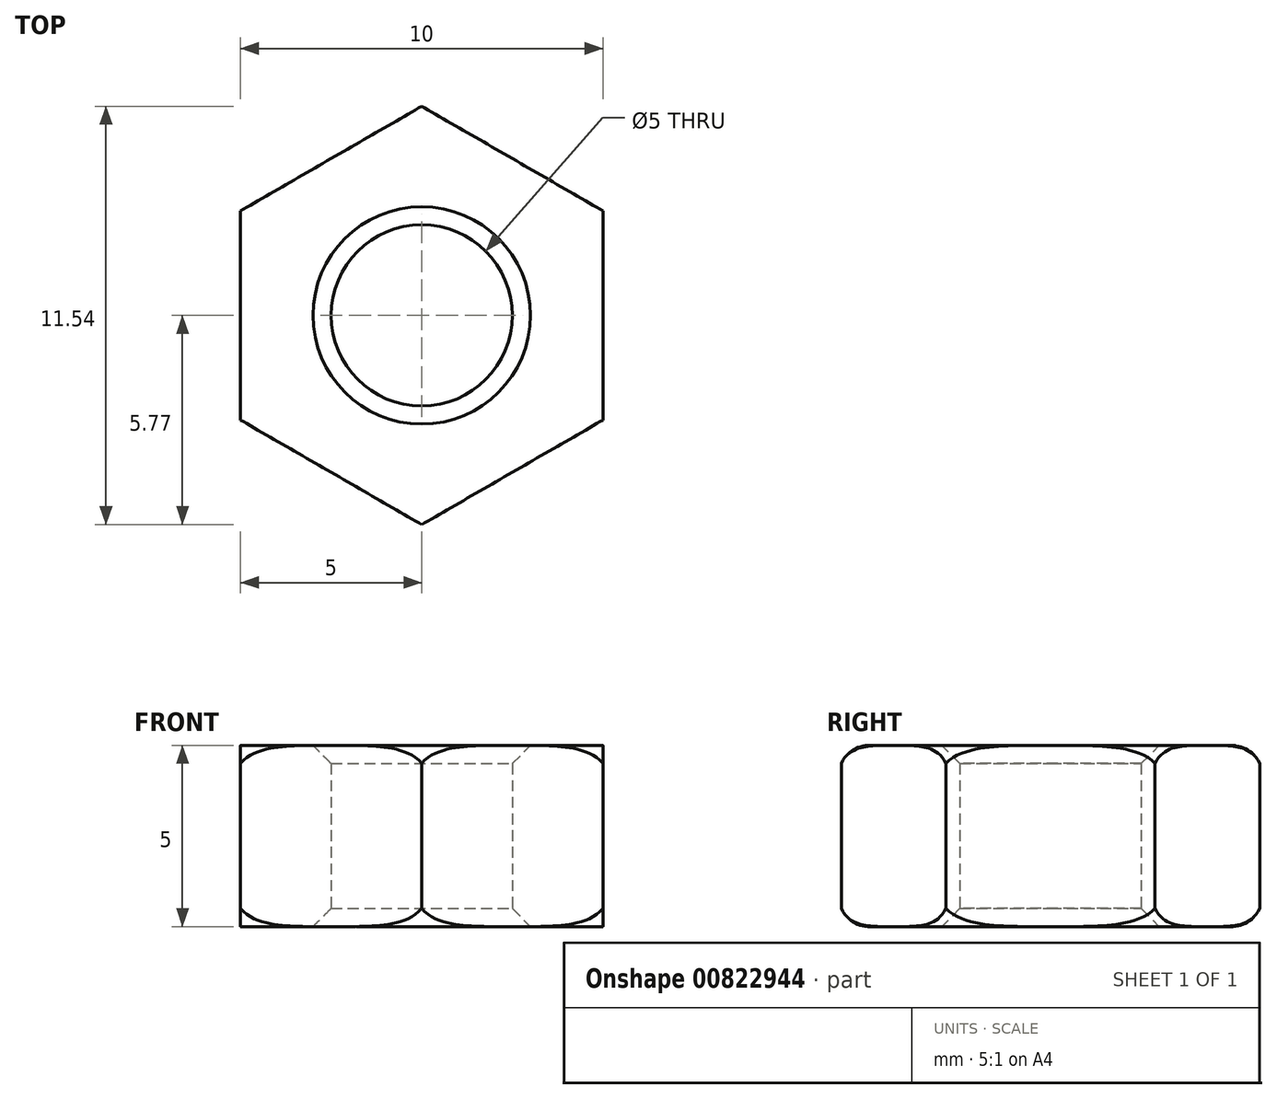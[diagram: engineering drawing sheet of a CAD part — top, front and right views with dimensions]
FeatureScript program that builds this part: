
annotation { "Feature Type Name" : "Feature", "Feature Type Description" : "" }
export const myFeature = defineFeature(function(context is Context, id is Id, definition is map)
    precondition{}
    {
        {
            var Q0;
            Q0=qCreatedBy(makeId("Front.planeOp"),FACE);
            var sketch = newSketch(context, id + "F0", { "sketchPlane" : qUnion([Q0])});
            skLineSegment(sketch, "E0", {"start": v(-2.5, 0) * mm, "end": v(-2.5, 2) * mm});
            skLineSegment(sketch, "E1", {"start": v(-2.5, 2) * mm, "end": v(-3, 2.5) * mm});
            skLineSegment(sketch, "E2", {"start": v(-3, 2.5) * mm, "end": v(-5, 2.5) * mm});
            skLineSegment(sketch, "E3", {"start": v(-5, 2.5) * mm, "end": v(-5.77, 2) * mm, "construction": true});
            skLineSegment(sketch, "E4", {"start": v(-5.77, 2) * mm, "end": v(-5.77, 0) * mm});
            skLineSegment(sketch, "E5", {"start": v(0, 0) * mm, "end": v(0, 8.86) * mm, "construction": true});
            skLineSegment(sketch, "E6", {"start": v(0, 0) * mm, "end": v(-2.5, 0) * mm, "construction": true});
            skLineSegment(sketch, "E7.MirrorCS", {"start": v(-2.5, -2) * mm, "end": v(-3, -2.5) * mm});
            skLineSegment(sketch, "E8.MirrorCS", {"start": v(-5.77, -2) * mm, "end": v(-5.77, 0) * mm});
            skLineSegment(sketch, "E9.MirrorCS", {"start": v(-5.77, 0) * mm, "end": v(-2.5, 0) * mm, "construction": true});
            skLineSegment(sketch, "E10.MirrorCS", {"start": v(-3, -2.5) * mm, "end": v(-5, -2.5) * mm});
            skLineSegment(sketch, "E11.MirrorCS", {"start": v(-5, -2.5) * mm, "end": v(-5.77, -2) * mm, "construction": true});
            skLineSegment(sketch, "E12.MirrorCS", {"start": v(-2.5, 0) * mm, "end": v(-2.5, -2) * mm});
            skLineSegment(sketch, "E13", {"start": v(-5, 2.5) * mm, "end": v(-5, -2.5) * mm, "construction": true});
            skCircle(sketch, "E14", {"center": v(0, 0) * mm, "radius": 5 * mm, "construction": true});
            skLineSegment(sketch, "E15", {"start": v(0, 0) * mm, "end": v(-10.5, -6.06) * mm, "construction": true});
            skLineSegment(sketch, "E16.0", {"start": v(-2.89, -5) * mm, "end": v(-5.77, 0) * mm, "construction": true});
            skLineSegment(sketch, "E16.1", {"start": v(-5.77, 0) * mm, "end": v(-2.89, 5) * mm, "construction": true});
            skLineSegment(sketch, "E16.2", {"start": v(-2.89, 5) * mm, "end": v(2.89, 5) * mm, "construction": true});
            skLineSegment(sketch, "E16.3", {"start": v(2.89, 5) * mm, "end": v(5.77, 0) * mm, "construction": true});
            skLineSegment(sketch, "E16.4", {"start": v(5.77, 0) * mm, "end": v(2.89, -5) * mm, "construction": true});
            skLineSegment(sketch, "E16.5", {"start": v(2.89, -5) * mm, "end": v(-2.89, -5) * mm, "construction": true});
            skPoint(sketch, "E16.0.midPoint", {"position": v(-4.33, -2.5) * mm});
            skArc(sketch, "E17", {"start": v(-5, 2.5) * mm, "mid": v(-5.46, 2.36) * mm, "end": v(-5.77, 2) * mm});
            skArc(sketch, "E18.MirrorCS", {"start": v(-5, -2.5) * mm, "mid": v(-5.46, -2.36) * mm, "end": v(-5.77, -2) * mm});
            skSolve(sketch);
        }
        {
            var Q0;
            Q0=makeQuery(id+"F0.imprint","IMPRINT",FACE,{"disambiguationData":[TD([[makeQuery(id+"F0.imprint","IMPRINT",EDGE,{"derivedFrom":sQuery(id+"F0.wireOp",EDGE,"E0")}),1.0]])]});
            var Q1;
            Q1=sQuery(id+"F0.wireOp",EDGE,"E5");
            revolve(context, id + "F1", {"surfaceOperationType" : NewSurfaceOperationType.NEW, "entities" : qUnion([Q0]), "axis" : qUnion([Q1]), "revolveType" : RevolveType.FULL});
        }
        {
            var Q0;
            Q0=qCreatedBy(makeId("Top.planeOp"),FACE);
            var sketch = newSketch(context, id + "F2", { "sketchPlane" : qUnion([Q0])});
            skCircle(sketch, "E19", {"center": v(0, 0) * mm, "radius": 5 * mm, "construction": true});
            skLineSegment(sketch, "E20", {"start": v(0, 0) * mm, "end": v(-0.78, 0) * mm, "construction": true});
            skLineSegment(sketch, "E21", {"start": v(0, 0) * mm, "end": v(5, 0) * mm, "construction": true});
            skLineSegment(sketch, "E22.0", {"start": v(5, 2.89) * mm, "end": v(5, -2.89) * mm});
            skLineSegment(sketch, "E22.1", {"start": v(5, -2.89) * mm, "end": v(0, -5.77) * mm});
            skLineSegment(sketch, "E22.2", {"start": v(0, -5.77) * mm, "end": v(-5, -2.89) * mm});
            skLineSegment(sketch, "E22.3", {"start": v(-5, -2.89) * mm, "end": v(-5, 2.89) * mm});
            skLineSegment(sketch, "E22.4", {"start": v(-5, 2.89) * mm, "end": v(0, 5.77) * mm});
            skLineSegment(sketch, "E22.5", {"start": v(0, 5.77) * mm, "end": v(5, 2.89) * mm});
            skPoint(sketch, "E22.0.midPoint", {"position": v(5, 0) * mm});
            skCircle(sketch, "E23", {"center": v(0, 0) * mm, "radius": 6.56 * mm});
            skSolve(sketch);
        }
        {
            var Q0;
            Q0=qSketchRegion(id+"F2",true);
            extrude(context, id + "F3", {"entities" : qUnion([Q0]), "operationType" : NewBodyOperationType.REMOVE, "endBound" : BoundingType.SYMMETRIC, "oppositeDirection" : true, "depth" : 25 * mm, "offsetDistance" : 25 * mm});
        }
    });
